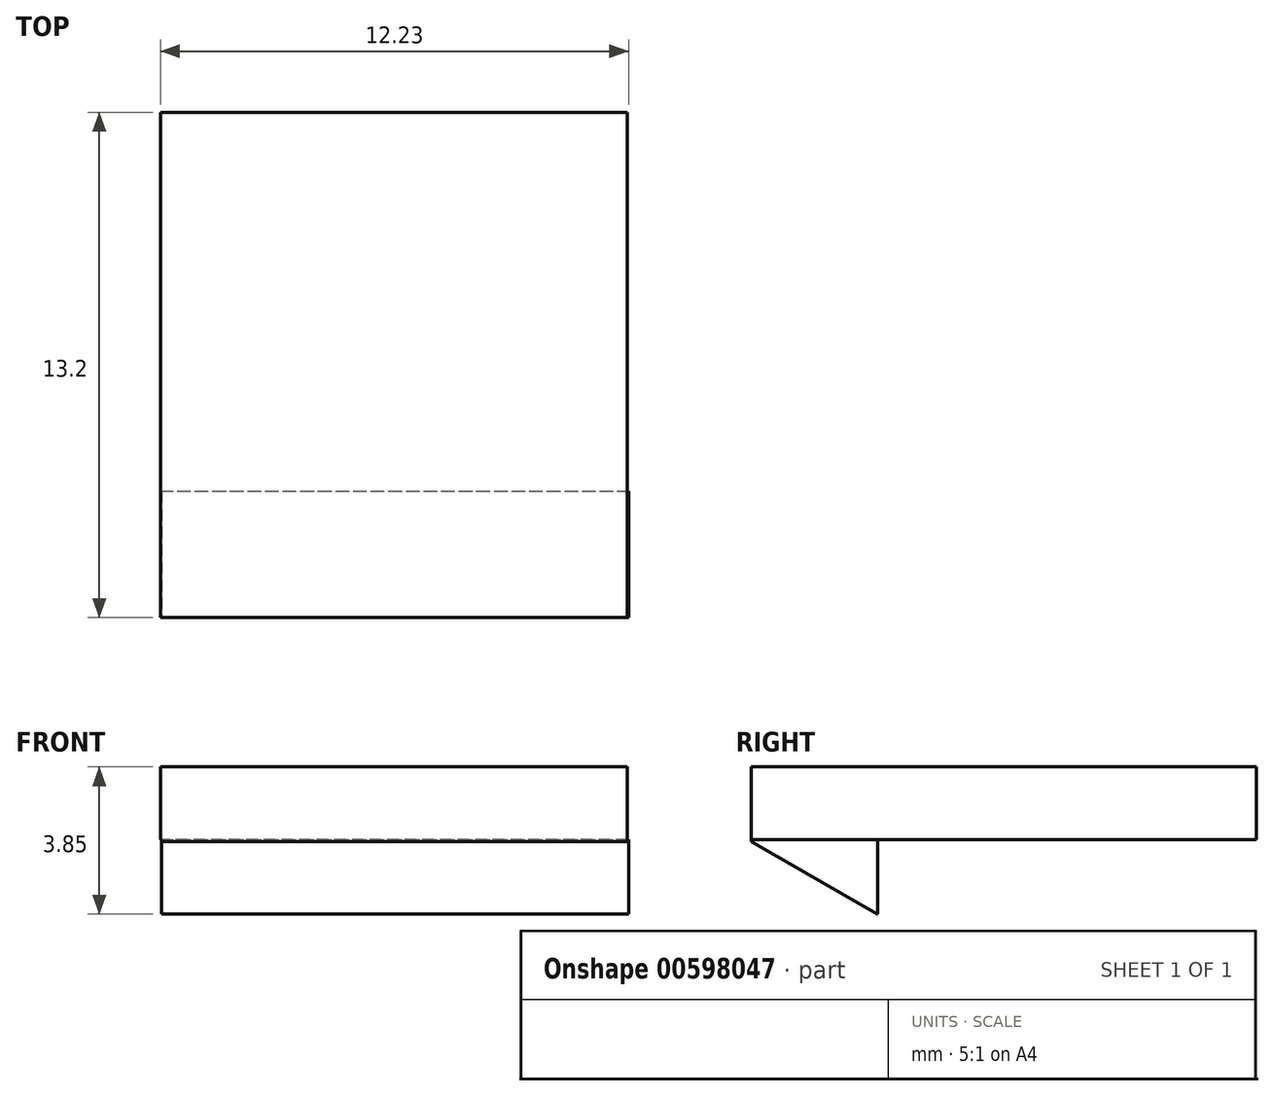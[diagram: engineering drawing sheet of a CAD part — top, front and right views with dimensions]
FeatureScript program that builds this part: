
annotation { "Feature Type Name" : "Feature", "Feature Type Description" : "" }
export const myFeature = defineFeature(function(context is Context, id is Id, definition is map)
    precondition{}
    {
        {
            var Q0;
            Q0=qCreatedBy(makeId("Top.planeOp"),FACE);
            var sketch = newSketch(context, id + "F0", { "sketchPlane" : qUnion([Q0])});
            skLineSegment(sketch, "E0.bottom", {"start": v(6.1, 6.6) * mm, "end": v(-6.1, 6.6) * mm});
            skLineSegment(sketch, "E0.top", {"start": v(6.1, -6.6) * mm, "end": v(-6.1, -6.6) * mm});
            skLineSegment(sketch, "E0.left", {"start": v(6.1, 6.6) * mm, "end": v(6.1, -6.6) * mm});
            skLineSegment(sketch, "E0.right", {"start": v(-6.1, 6.6) * mm, "end": v(-6.1, -6.6) * mm});
            skPoint(sketch, "E0.middle", {"position": v(0, 0) * mm});
            skSolve(sketch);
        }
        {
            var Q0;
            Q0 = qSketchRegion(id + "F0", true);
            extrude(context, id + "F1", {"entities" : qUnion([Q0]), "depth" : 1.9 * mm, "offsetDistance" : 25 * mm});
        }
        {
            var Q0;
            Q0=qCreatedBy(makeId("Top.planeOp"),FACE);
            var sketch = newSketch(context, id + "F2", { "sketchPlane" : qUnion([Q0])});
            skLineSegment(sketch, "E1.bottom", {"start": v(-6.07, -6.6) * mm, "end": v(6.13, -6.6) * mm});
            skLineSegment(sketch, "E1.top", {"start": v(-6.07, -3.3) * mm, "end": v(6.13, -3.3) * mm});
            skLineSegment(sketch, "E1.left", {"start": v(-6.07, -6.6) * mm, "end": v(-6.07, -3.3) * mm});
            skLineSegment(sketch, "E1.right", {"start": v(6.13, -6.6) * mm, "end": v(6.13, -3.3) * mm});
            skSolve(sketch);
        }
        {
            var Q0;
            Q0 = qSketchRegion(id + "F2", true);
            extrude(context, id + "F3", {"entities" : qUnion([Q0]), "operationType" : NewBodyOperationType.ADD, "oppositeDirection" : true, "depth" : 1.95 * mm, "offsetDistance" : 25 * mm});
        }
        {
            var Q0;
            Q0=makeQuery(id+"F3.opExtrude","CAP_EDGE",EDGE,{"disambiguationData":[OSD([sQuery(id+"F2.wireOp",EDGE,"E1.bottom")])],"isStart":false});
            chamfer(context, id + "F4", {"entities" : qUnion([Q0]), "chamferType" : ChamferType.OFFSET_ANGLE, "width" : 1.9 * mm, "oppositeDirection" : false, "angle" : 60 * degree, "tangentPropagation" : true});
        }
    });
